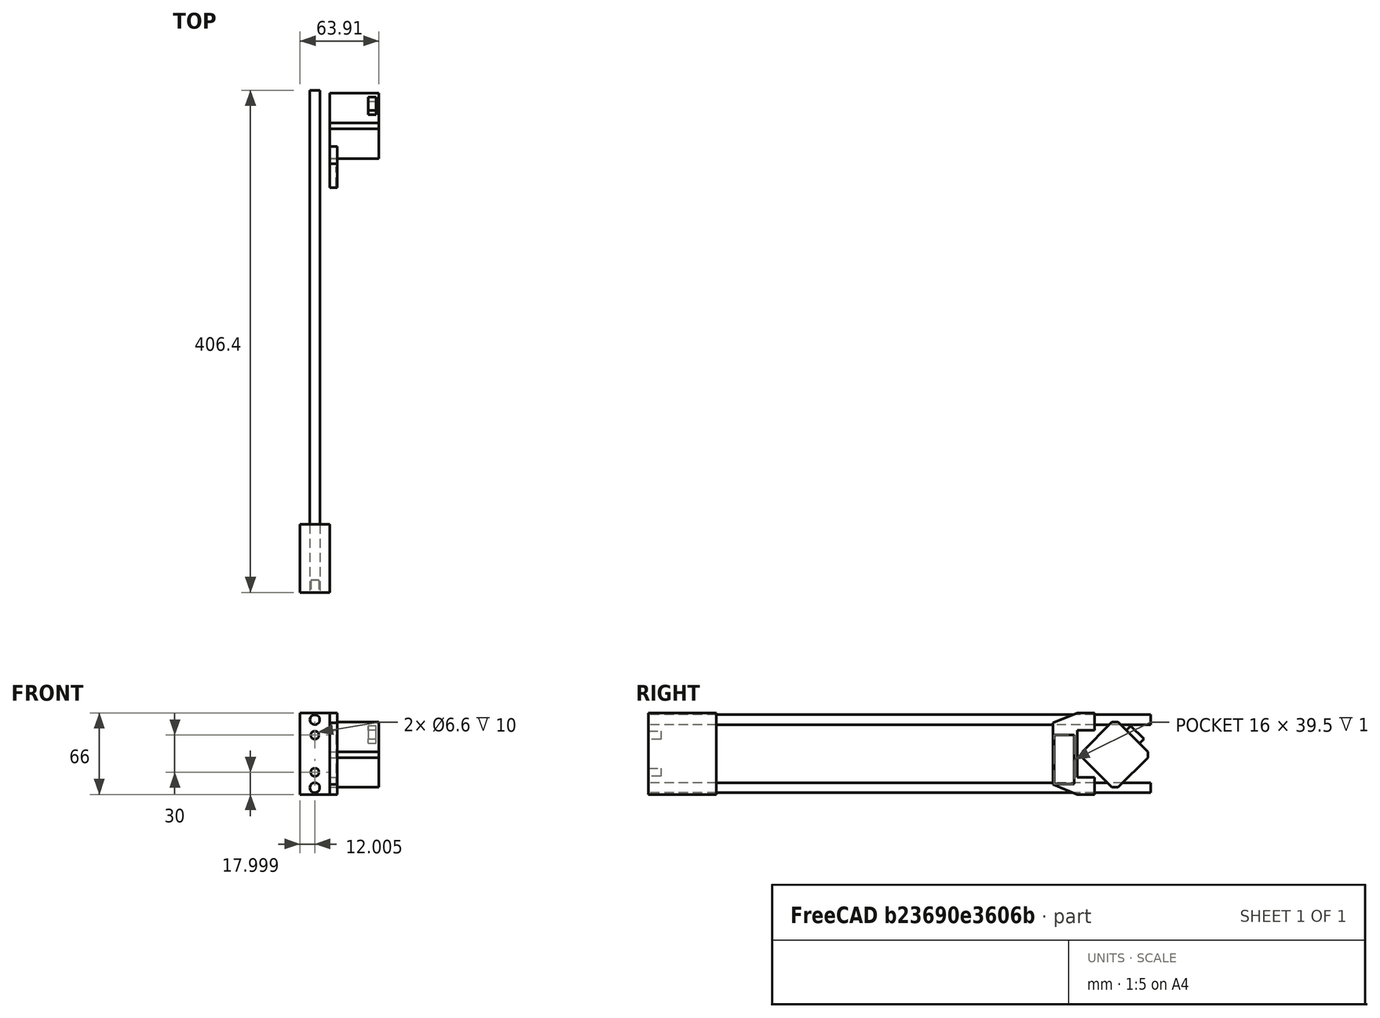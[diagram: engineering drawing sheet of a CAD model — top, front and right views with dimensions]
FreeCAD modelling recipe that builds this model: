
FCSTD DOCUMENT  (FreeCAD 0.16R6705 (Git))
Label: D3D_Circuit_Mill_Y_Axis
License: All rights reserved
LicenseURL: http://en.wikipedia.org/wiki/All_rights_reserved
objects: PartDesign::Pocket×3, Part::Cylinder×2, Part::Feature×2, PartDesign::Pad×1, App::DocumentObjectGroup×1
note: 12 computed .brp shape members not serialized (recipe doc carries the construction recipe); baked Part::Feature solids carry a one-line shape summary decoded from their .brp

FEATURE [PartDesign::Pad] Pad001
  Length = 5
  Length2 = 100
  Placement = pos=(0.155147,-33.3147,-62.0829) rot=(0.707107,0,0.707107;3.14159rad)
  Type = 0
FEATURE [PartDesign::Pocket] Pocket
  Length = 10
  Placement = pos=(-23.8449,-22.413,-47.4564) rot=(-0.57735,0.57735,-0.57735;2.0944rad)
  Type = 0
FEATURE [Part::Cylinder] Cylinder
  Angle = 360
  Height = 406.4
  Placement = pos=(-11.8449,-4.47833,-33.731) rot=(0,-0.707107,0.707107;3.14159rad)
  Radius = 4
FEATURE [Part::Feature] Fusion001  label="D3D End Stop Interface simple001"
  Placement = pos=(0.155147,-36.4783,-61.231) rot=(-0.57735,0.57735,-0.57735;2.0944rad)
  shape: bbox 6 x 33.5 x 66 mm, 17 faces (baked)
FEATURE [PartDesign::Pocket] Pocket002
  Length = 60
  Placement = pos=(-23.4861,-188.232,-66.0258) rot=(-0.57735,0.57735,-0.57735;2.0944rad)
  Type = 0
FEATURE [Part::Cylinder] Cylinder001
  Angle = 360
  Height = 406.4
  Placement = pos=(-11.8449,-4.47833,-88.731) rot=(0,-0.707107,0.707107;3.14159rad)
  Radius = 4
FEATURE [PartDesign::Pocket] Pocket003
  Length = 100
  Type = 0
FEATURE [Part::Feature] Pocket006
  Placement = pos=(0.151941,-409.332,-47.4564) rot=(-0.57735,-0.57735,0.57735;2.0944rad)
  shape: bbox 24 x 55 x 66 mm, 10 faces (baked)
FEATURE [App::DocumentObjectGroup] Construction
